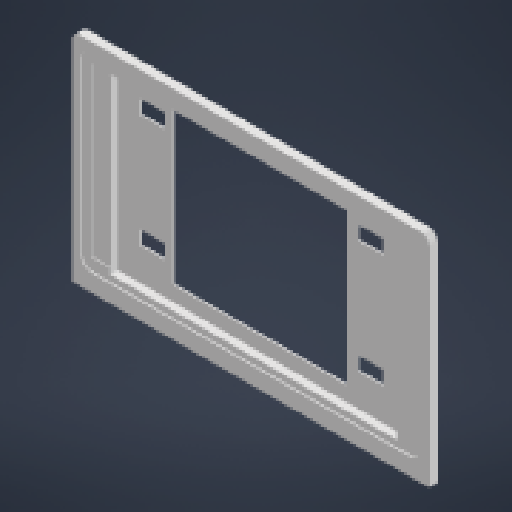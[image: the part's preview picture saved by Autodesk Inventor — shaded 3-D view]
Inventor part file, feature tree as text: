
AUTODESK INVENTOR PART (.ipt)
format: ipt  version: 2024 (Build 280153000, 153)  size: 246,784 bytes
history: native  units: mm
features: projected_geometry x7, extrude x6, sketch x6, other x4, reference x1
ambient origin geometry x8: Origin, YZ Plane, XZ Plane, XY Plane, X Axis, Y Axis, Z Axis, Center Point
bodies: Body1 (feature_tree)
feature tree (24):
  other  "솔리드1"
  extrude  "돌출1"  Depth=5.0mm TaperAngle=0.0deg
  extrude  "돌출2"  Depth=197.0mm
  sketch  "스케치3"
  extrude  "돌출4"  Depth=111.0mm
  extrude  "돌출5"  Depth=207.0mm
  extrude  "돌출6"  Depth=126.0mm
  extrude  "돌출8"  Depth=103.5mm
  sketch  "스케치1"
  reference  "참조1"
  sketch  "스케치2"
  projected_geometry  "투영된 루프1"
  projected_geometry  "투영된 루프2"
  sketch  "스케치4"
  projected_geometry  "투영된 루프3"
  sketch  "스케치6"
  projected_geometry  "투영된 루프4"
  sketch  "스케치8"
  projected_geometry  "투영된 루프5"
  projected_geometry  "투영된 루프6"
  projected_geometry  "투영된 루프7"
  other  "<userpath>\Downloads\AAST\PART\AAST Remote Controler\AASTRC case.iam"
  other  "AASTRC case.iam"
  other  "AASTRC Bottom case:1"
